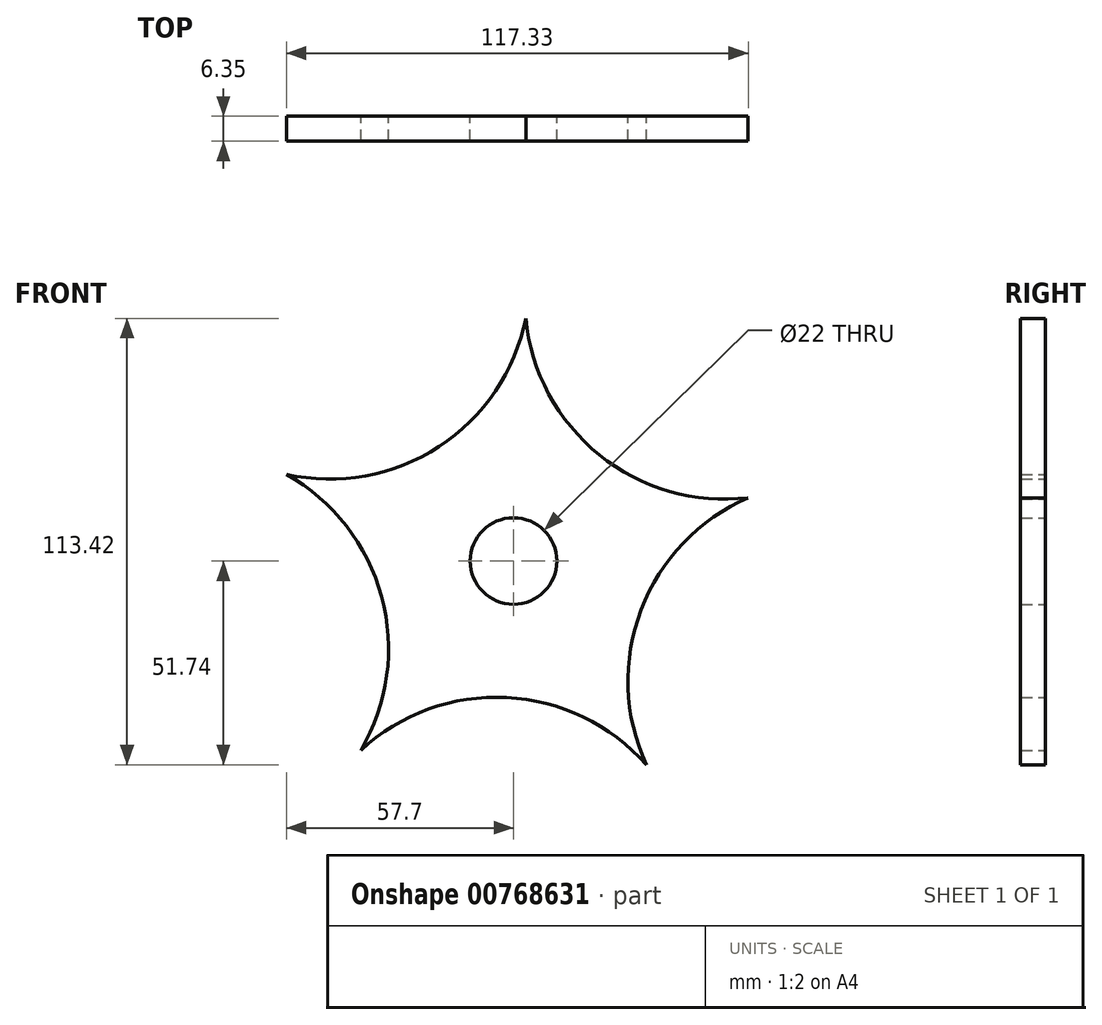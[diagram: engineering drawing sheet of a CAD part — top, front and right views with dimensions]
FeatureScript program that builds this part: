
annotation { "Feature Type Name" : "Feature", "Feature Type Description" : "" }
export const myFeature = defineFeature(function(context is Context, id is Id, definition is map)
    precondition{}
    {
        {
            var Q0;
            Q0=qCreatedBy(makeId("Front.planeOp"),FACE);
            var sketch = newSketch(context, id + "F0", { "sketchPlane" : qUnion([Q0])});
            skCircle(sketch, "E0", {"center": v(0, 0) * mm, "radius": 11 * mm});
            skArc(sketch, "E1", {"start": v(-57.7, 22.03) * mm, "mid": v(-18.95, 29.07) * mm, "end": v(3.12, 61.68) * mm});
            skArc(sketch, "E2", {"start": v(3.12, 61.68) * mm, "mid": v(21.79, 27) * mm, "end": v(59.63, 16.1) * mm});
            skArc(sketch, "E3", {"start": v(-38.78, -48.07) * mm, "mid": v(-33.5, -9.04) * mm, "end": v(-57.7, 22.03) * mm});
            skArc(sketch, "E4", {"start": v(33.73, -51.74) * mm, "mid": v(-1.75, -34.66) * mm, "end": v(-38.78, -48.07) * mm});
            skArc(sketch, "E5", {"start": v(59.63, 16.1) * mm, "mid": v(32.42, -12.38) * mm, "end": v(33.73, -51.74) * mm});
            skSolve(sketch);
        }
        {
            var Q0;
            Q0=makeQuery(id+"F0.imprint","IMPRINT",FACE,{"disambiguationData":[TD([[makeQuery(id+"F0.imprint","IMPRINT",EDGE,{"derivedFrom":sQuery(id+"F0.wireOp",EDGE,"E0")}),-1.0]])]});
            extrude(context, id + "F1", {"entities" : qUnion([Q0]), "depth" : 6.35 * mm, "offsetDistance" : 25.4 * mm});
        }
    });
